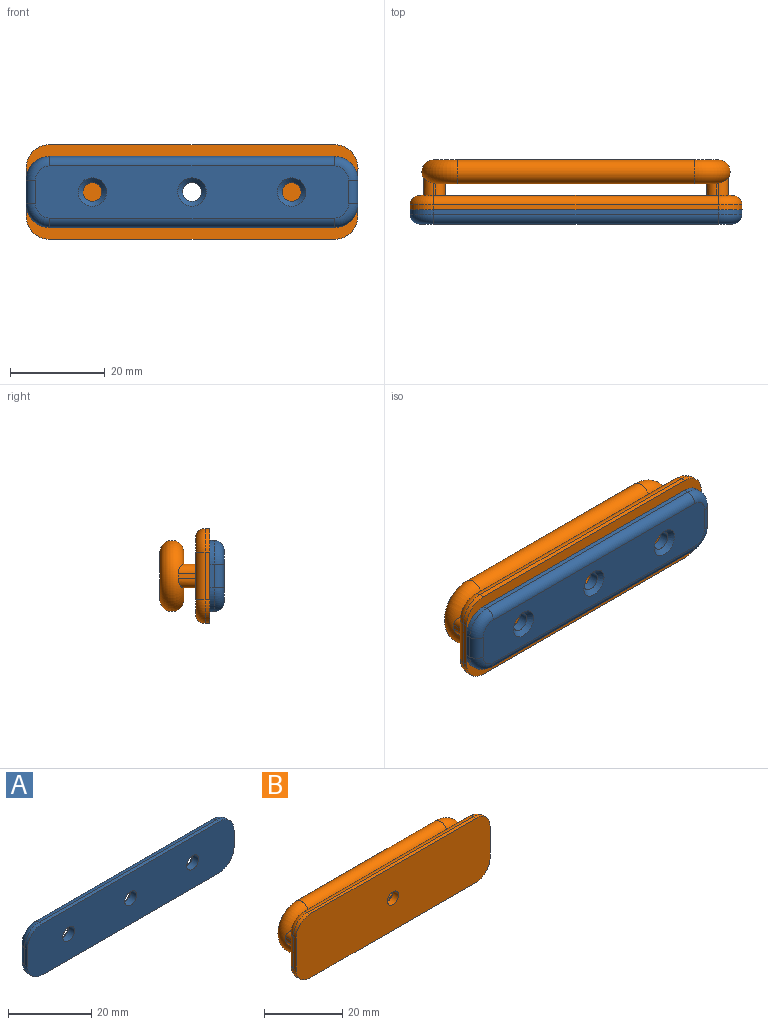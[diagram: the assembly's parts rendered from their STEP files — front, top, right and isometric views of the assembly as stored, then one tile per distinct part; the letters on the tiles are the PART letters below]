
ASSEMBLY  parts=2 mates=1
PART A: 24 faces, bbox 70.8x3.4x15.8 mm
  f0: plane 5x1mm, normal (-1,0,0), area 5mm2, adj f4,f12,f15,f19
  f1: plane 60x1mm, normal (0,0,-1), area 60mm2, adj f4,f12,f13,f16
  f2: plane 5x1mm, normal (1,0,0), area 5mm2, adj f4,f13,f14,f20
  f3: plane 60x1mm, normal (0,0,1), area 60mm2, adj f4,f14,f15,f23
  f4: plane 70x15mm, normal (0,-1,0), area 990.8mm2, adj f0,f1,f2,f3,f6,f8,f10,f12
  f5: plane 66x11mm, normal (0,1,0), area 633.5mm2, adj f7,f9,f11,f16,f17,f18,f19,f20
  f6: cylinder r=2mm len=4mm, axis (0,1,0), area 25.1mm2, adj f4,f7
  f7: cone r=2mm half-angle=45deg, axis (0,1,0), area 22.2mm2, adj f5,f6
  f8: cylinder r=2mm len=4mm, axis (0,1,0), area 25.1mm2, adj f4,f9
  f9: cone r=2mm half-angle=45deg, axis (0,1,0), area 22.2mm2, adj f5,f8
  f10: cylinder r=2mm len=4mm, axis (0,1,0), area 25.1mm2, adj f4,f11
  f11: cone r=2mm half-angle=45deg, axis (0,1,0), area 22.2mm2, adj f5,f10
  f12: cylinder r=5mm len=5mm, axis (0,-1,0), area 7.9mm2, adj f0,f1,f4,f17
  f13: cylinder r=5mm len=5mm, axis (0,1,0), area 7.9mm2, adj f1,f2,f4,f18
  f14: cylinder r=5mm len=5mm, axis (0,-1,0), area 7.9mm2, adj f2,f3,f4,f22
  f15: cylinder r=5mm len=5mm, axis (0,1,0), area 7.9mm2, adj f0,f3,f4,f21
  f16: cylinder r=2mm len=60mm, axis (1,0,0), area 188.5mm2, adj f1,f5,f17,f18
  f17: torus R=3mm, axis (0,-1,0), area 21.1mm2, adj f5,f12,f16,f19
  f18: torus R=3mm, axis (0,-1,0), area 21.1mm2, adj f5,f13,f16,f20
  f19: cylinder r=2mm len=5mm, axis (0,0,-1), area 15.7mm2, adj f0,f5,f17,f21
  f20: cylinder r=2mm len=5mm, axis (0,0,1), area 15.7mm2, adj f2,f5,f18,f22
  f21: torus R=3mm, axis (0,-1,0), area 21.1mm2, adj f5,f15,f19,f23
  f22: torus R=3mm, axis (0,-1,0), area 21.1mm2, adj f5,f14,f20,f23
  f23: cylinder r=2mm len=60mm, axis (-1,0,0), area 188.5mm2, adj f3,f5,f21,f22
PART B: 40 faces, bbox 70.8x10.9x20.8 mm
  f0: torus R=5mm, axis (0,1,0), area 224.3mm2, adj f1,f3,f8,f9,f10,f11,f16,f17
  f1: cylinder r=2.5mm len=50mm, axis (-1,0,0), area 785.4mm2, adj f0,f2
  f2: torus R=5mm, axis (0,1,0), area 224.3mm2, adj f1,f3,f4,f5,f6,f7,f12,f13
  f3: cylinder r=2.5mm len=50mm, axis (1,0,0), area 785.4mm2, adj f0,f2
  f4: plane 2.61x0.51mm, normal (0,0,-1), area 1.3mm2, adj f2,f13,f15,f20
  f5: plane 3.67x1mm, normal (1,0,0), area 3.7mm2, adj f2,f14,f15,f20
  f6: plane 2.61x0.51mm, normal (0,0,1), area 1.3mm2, adj f2,f12,f14,f20
  f7: plane 4.3x1mm, normal (-1,0,0), area 4.2mm2, adj f2,f12,f13,f20
  f8: plane 2.61x0.51mm, normal (0,0,-1), area 1.3mm2, adj f0,f17,f18,f20
  f9: plane 4.3x1mm, normal (1,0,0), area 4.2mm2, adj f0,f16,f17,f20
  f10: plane 2.61x0.51mm, normal (0,0,1), area 1.3mm2, adj f0,f16,f19,f20
  f11: plane 3.67x1mm, normal (-1,0,0), area 3.7mm2, adj f0,f18,f19,f20
  f12: cylinder r=2mm len=4.15mm, axis (0,-1,0), area 9.5mm2, adj f2,f6,f7,f20
  f13: cylinder r=2mm len=4.15mm, axis (0,1,0), area 9.5mm2, adj f2,f4,f7,f20
  f14: cylinder r=2mm len=3.68mm, axis (0,1,0), area 10.1mm2, adj f2,f5,f6,f20
  f15: cylinder r=2mm len=3.68mm, axis (0,-1,0), area 10.1mm2, adj f2,f4,f5,f20
  f16: cylinder r=2mm len=4.15mm, axis (0,-1,0), area 9.5mm2, adj f0,f9,f10,f20
  f17: cylinder r=2mm len=4.15mm, axis (0,1,0), area 9.5mm2, adj f0,f8,f9,f20
  f18: cylinder r=2mm len=3.68mm, axis (0,-1,0), area 10.1mm2, adj f0,f8,f11,f20
  f19: cylinder r=2mm len=3.68mm, axis (0,1,0), area 10.1mm2, adj f0,f10,f11,f20
  f20: plane 66x16mm, normal (0,1,0), area 981.9mm2, adj f4,f5,f6,f7,f8,f9,f10,f11
  f21: plane 60x1mm, normal (0,0,1), area 60mm2, adj f25,f26,f29,f37
  f22: plane 10x1mm, normal (-1,0,0), area 10mm2, adj f25,f26,f27,f33
  f23: plane 60x1mm, normal (0,0,-1), area 60mm2, adj f25,f27,f28,f30
  f24: plane 10x1mm, normal (1,0,0), area 10mm2, adj f25,f28,f29,f34
  f25: plane 70x20mm, normal (0,-1,0), area 1366mm2, adj f21,f22,f23,f24,f26,f27,f28,f29
  f26: cylinder r=5mm len=5mm, axis (0,-1,0), area 7.9mm2, adj f21,f22,f25,f35
  f27: cylinder r=5mm len=5mm, axis (0,1,0), area 7.9mm2, adj f22,f23,f25,f31
  f28: cylinder r=5mm len=5mm, axis (0,-1,0), area 7.9mm2, adj f23,f24,f25,f32
  f29: cylinder r=5mm len=5mm, axis (0,1,0), area 7.9mm2, adj f21,f24,f25,f36
  f30: cylinder r=2mm len=60mm, axis (1,0,0), area 188.5mm2, adj f20,f23,f31,f32
  f31: torus R=3mm, axis (0,-1,0), area 21.1mm2, adj f20,f27,f30,f33
  f32: torus R=3mm, axis (0,-1,0), area 21.1mm2, adj f20,f28,f30,f34
  f33: cylinder r=2mm len=10mm, axis (0,0,-1), area 31.4mm2, adj f20,f22,f31,f35
  f34: cylinder r=2mm len=10mm, axis (0,0,1), area 31.4mm2, adj f20,f24,f32,f36
  f35: torus R=3mm, axis (0,-1,0), area 21.1mm2, adj f20,f26,f33,f37
  f36: torus R=3mm, axis (0,-1,0), area 21.1mm2, adj f20,f29,f34,f37
  f37: cylinder r=2mm len=60mm, axis (-1,0,0), area 188.5mm2, adj f20,f21,f35,f36
  f38: cylinder r=2mm len=4mm, axis (0,1,0), area 25.1mm2, adj f25,f39
  f39: cone r=2mm half-angle=45deg, axis (0,1,0), area 22.2mm2, adj f20,f38
PLACE A rot(axis=(1,0,0),180deg) t=(21.86,-89.91,-16.71)mm
PLACE B rot(axis=(-0.11,0.93,0.34),0deg) t=(22.22,-45.91,-1.96)mm
MATE revolute B.f38 <-> A.f8  axis (0,-1,0) through (29.51,-53.91,-6.96)mm
